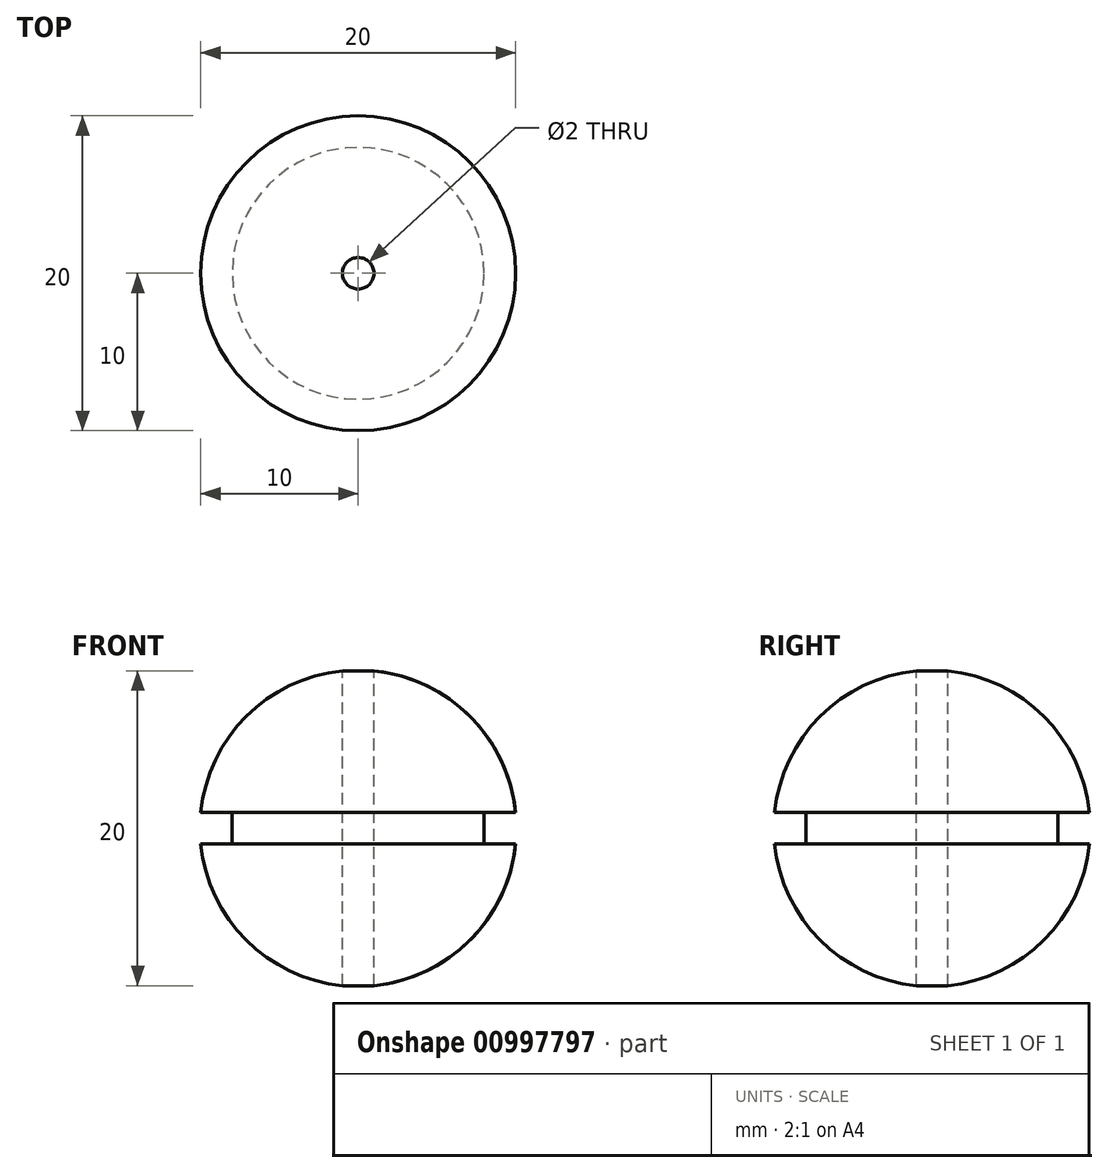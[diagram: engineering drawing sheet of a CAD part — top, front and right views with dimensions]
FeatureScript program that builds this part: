
annotation { "Feature Type Name" : "Feature", "Feature Type Description" : "" }
export const myFeature = defineFeature(function(context is Context, id is Id, definition is map)
    precondition{}
    {
        {
            var Q0;
            Q0=qCreatedBy(makeId("Front.planeOp"),FACE);
            var sketch = newSketch(context, id + "F0", { "sketchPlane" : qUnion([Q0])});
            skLineSegment(sketch, "E0", {"start": v(0, 10) * mm, "end": v(0, -10) * mm});
            skPoint(sketch, "E1.endSnap0", {"position": v(-10, 0) * mm});
            skLineSegment(sketch, "E2", {"start": v(-8, 0) * mm, "end": v(-8, 1) * mm});
            skLineSegment(sketch, "E3", {"start": v(-8, 0) * mm, "end": v(-8, -1) * mm});
            skArc(sketch, "E4", {"start": v(-1, -10) * mm, "mid": v(-10.05, 0) * mm, "end": v(-1, 10) * mm});
            skLineSegment(sketch, "E5", {"start": v(-1, 10) * mm, "end": v(-1, -10) * mm});
            skLineSegment(sketch, "E6", {"start": v(-8, -1) * mm, "end": v(-10, -1) * mm});
            skLineSegment(sketch, "E7", {"start": v(-8, 1) * mm, "end": v(-10, 1) * mm});
            skSolve(sketch);
        }
        {
            var Q0;
            Q0=makeQuery(id+"F0.imprint","IMPRINT",FACE,{"disambiguationData":[TD([[makeQuery(id+"F0.imprint","IMPRINT",EDGE,{"derivedFrom":sQuery(id+"F0.wireOp",EDGE,"E2")}),-1.0]])]});
            var Q1;
            Q1=sQuery(id+"F0.wireOp",EDGE,"E0");
            revolve(context, id + "F1", {"surfaceOperationType" : NewSurfaceOperationType.NEW, "entities" : qUnion([Q0]), "axis" : qUnion([Q1]), "revolveType" : RevolveType.FULL});
        }
    });
